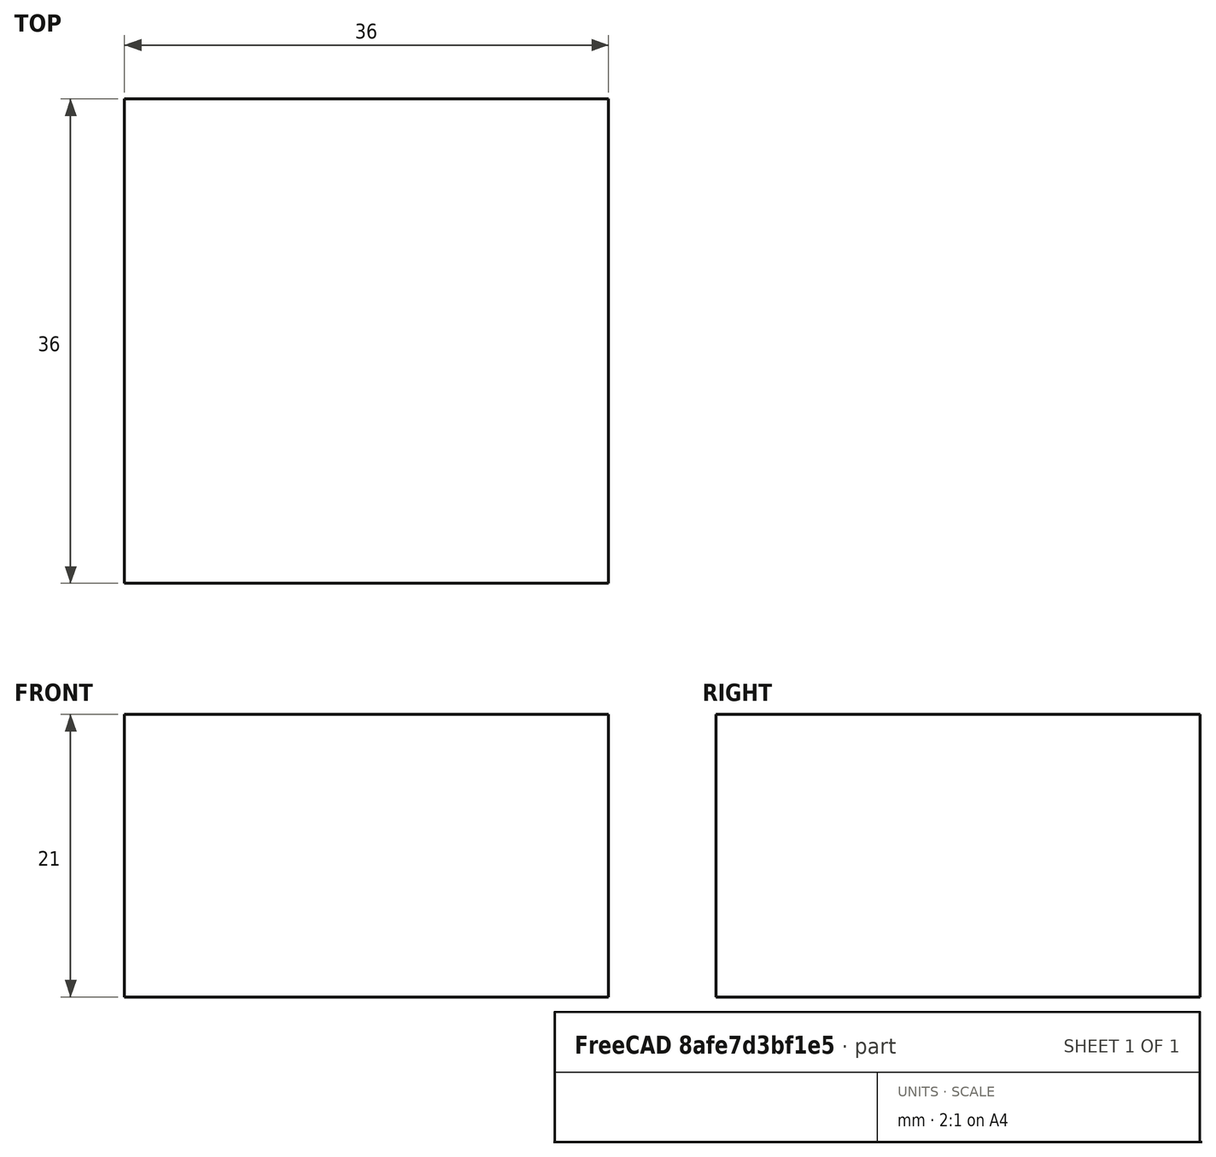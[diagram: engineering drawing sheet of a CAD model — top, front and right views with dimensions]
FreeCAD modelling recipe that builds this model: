
FCSTD DOCUMENT  (FreeCAD 0.18R16033 (Git))
Label: fc_stack_simple
License: All rights reserved
LicenseURL: http://en.wikipedia.org/wiki/All_rights_reserved
objects: Sketcher::SketchObject×1, PartDesign::Pad×1, PartDesign::Body×1
note: 4 computed .brp shape members not serialized (recipe doc carries the construction recipe); baked Part::Feature solids carry a one-line shape summary decoded from their .brp

FEATURE [Sketcher::SketchObject] Sketch
  MapMode = 5
  Support = -> [XY_Plane]
  sketch-geometry (4):
    g0: LineSegment StartX=-18 StartY=18 StartZ=0 EndX=18 EndY=18 EndZ=0
    g1: LineSegment StartX=18 StartY=18 StartZ=0 EndX=18 EndY=-18 EndZ=0
    g2: LineSegment StartX=18 StartY=-18 StartZ=0 EndX=-18 EndY=-18 EndZ=0
    g3: LineSegment StartX=-18 StartY=-18 StartZ=0 EndX=-18 EndY=18 EndZ=0
  constraints (10):
    c: Coincident(g0,g1)
    c: Coincident(g1,g2)
    c: Coincident(g2,g3)
    c: Coincident(g3,g0)
    c: Horizontal(g2)
    c: Vertical(g3)
    c: Symmetric(g0,g0,g-2)
    c: Symmetric(g0,g1,g-1)
    c: DistanceY(g1,g1) = 36
    c: DistanceX(g2,g2) = 36
FEATURE [PartDesign::Pad] Pad
  Length = 21
  Length2 = 100
  Profile = -> Sketch
  Type = 0
FEATURE [PartDesign::Body] Body
  Group = -> [Sketch,Pad]
  Origin = -> Origin
  Tip = -> Pad
